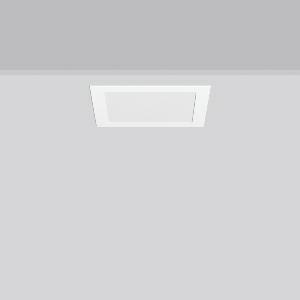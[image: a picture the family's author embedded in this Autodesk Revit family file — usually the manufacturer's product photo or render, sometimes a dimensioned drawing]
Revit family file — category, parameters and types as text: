
# Revit family: toledo_flat_square_e_901670_002_730_51d1
name_source: partatom
category: Lighting Fixtures
units: mm (PartAtom-declared; Revit-internal decimal feet)

## family parameters
Cut with Voids When Loaded = No
Host = Face
Light Source = No
Part Type = Normal
Room Calculation Point = No
Round Connector Dimension = Use Diameter
Shared = No

## types (1)
- TuneableWhite 846 (1 x LED Modul 846, 1600 lm, 4600)
    Apparent Load = 19 VA
    CIE Flux Codes = 48 79 96 100 100
    Color Rendering = 80
    Color Temperature = 4600
    Default Elevation = 1800 mm
    Description = Series: TOLEDO FLAT square
Ultra thin recessed downlight. Housing: die-cast aluminium. Light guide and diffuser made of non-yellowing PMMA, opal matt. Tunable white dynamically adjustable from 2700 K to 6500 K.With Casambi smart+free Bluetooth control for wireless network and operation using Android / iOS devices, free app available for download. Ceiling installation with spring system. Mounting depth depends on ceiling strength. Surface mounted housing as accessory for all sizes. Retrofittable decorative cylinders made of chintz fabric as accessory, optional with satin finish plastic diffuser. Through-wiring box (5 pole) available as accessory. 
Colour: white
Length: 225 mm
Width: 225 mm
Height: 3 mm
Cut-out length: 208 mm
Cut-out width: 208 mm
Recess height: 55-75 mm
Luminaire: recess height: 31-51 mm
Lamp: LED
Socket: without socket
Colour temperature: 2700K - 6500K
Colour rendering index (CRI): 80
System power: 19 W
Rated luminous flux: 1600 lm
Luminous efficiency: 84 lm/W
System power 2: 20 W
Rated luminous flux 2: 1500 lm
Luminous efficiency 2: 75 lm/W
System power 3: 18 W
Rated luminous flux 3: 1550 lm
Luminous efficiency 3: 86 lm/W
Control gear: Dimmable Bluetooth converter
Protection class: II
Type of protection: IP 54
    Height = 0 mm  [stored 0 ft]
    Lamp = 1 x LED Modul 846
    Lamp Light Flux = 1600 lm
    Lamp count = 1
    Length = 225 mm
    Lifetime = 50000 h
    Luminous efficacy = 84 lm/W
    Manufacturer = RZB
    ModVariant = No
    Model = 901670.002.730
    Mounting Place = Ceiling
    Mounting Type = Recessed
    Number of Poles = 1
    OnlyDefault = Yes
    Power Factor = 1
    Product Name = TOLEDO FLAT square E
    Product group = Recessed downlights
    ProductGroupID = 402
    Protection Class = Protection class II
    Protection Degree = IP 40
    RLX_Detail_Level = 1
    RLX_Emergency_Light_Flux = 0 lm
    RLX_Emergency_Type = 0
    RLX_Emergency_Type_DB = No
    RlxData = <blob elided: 58501 chars, md5=7632c253>
    Socket = socket
    Standby Power = 0 W
    System Light Flux = 1600 lm
    System Power = 19 W
    Type Comments = TuneableWhite 846
    Type Image = 901487.002.jpg
    URL = http://relux.com
    VarID = tuneablewhite_846
    Voltage = 230 V
    Voltage Range = 220-240 V
    Weight = 0.00 kg
    Width = 225 mm

note: [stored X ft] marks values corroborated as IEEE doubles in the binary element streams (Revit-internal decimal feet)

## geometry (parser evidence)
native form markers: Blend x4, Sweep x9
no freeform markers — native parametric forms only
